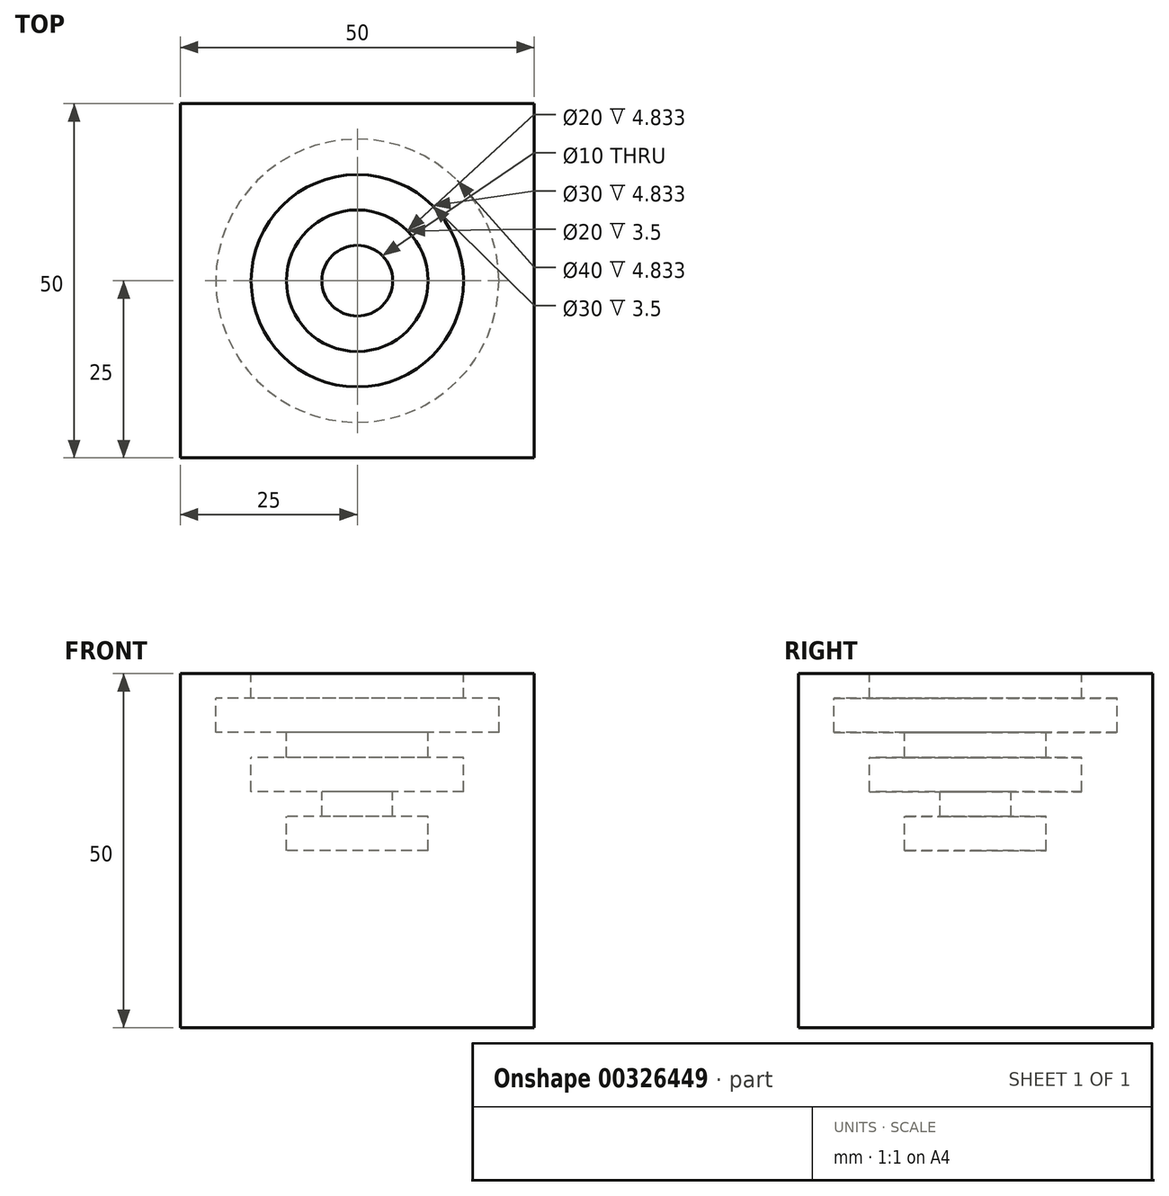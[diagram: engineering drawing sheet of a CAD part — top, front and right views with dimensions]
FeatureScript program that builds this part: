
annotation { "Feature Type Name" : "Feature", "Feature Type Description" : "" }
export const myFeature = defineFeature(function(context is Context, id is Id, definition is map)
    precondition{}
    {
        {
            var Q0;
            Q0=qCreatedBy(makeId("Top.planeOp"),FACE);
            var sketch = newSketch(context, id + "F0", { "sketchPlane" : qUnion([Q0])});
            skLineSegment(sketch, "E0.bottom", {"start": v(25, -25) * mm, "end": v(-25, -25) * mm});
            skLineSegment(sketch, "E0.top", {"start": v(25, 25) * mm, "end": v(-25, 25) * mm});
            skLineSegment(sketch, "E0.left", {"start": v(25, -25) * mm, "end": v(25, 25) * mm});
            skLineSegment(sketch, "E0.right", {"start": v(-25, -25) * mm, "end": v(-25, 25) * mm});
            skPoint(sketch, "E0.middle", {"position": v(0, 0) * mm});
            skSolve(sketch);
        }
        {
            var Q0;
            Q0=makeQuery(id+"F0.imprint","IMPRINT",FACE,{"disambiguationData":[TD([[makeQuery(id+"F0.imprint","IMPRINT",EDGE,{"derivedFrom":sQuery(id+"F0.wireOp",EDGE,"E0.bottom")}),-1.0]])]});
            extrude(context, id + "F1", {"entities" : qUnion([Q0]), "endBound" : BoundingType.SYMMETRIC, "depth" : 50 * mm});
        }
        {
            var Q0;
            Q0=qCreatedBy(makeId("Front.planeOp"),FACE);
            var sketch = newSketch(context, id + "F2", { "sketchPlane" : qUnion([Q0])});
            skLineSegment(sketch, "E1", {"start": v(0, 0) * mm, "end": v(0, 25) * mm});
            skLineSegment(sketch, "E2", {"start": v(0, 25) * mm, "end": v(15, 25) * mm});
            skLineSegment(sketch, "E3", {"start": v(15, 25) * mm, "end": v(15, 21.5) * mm});
            skLineSegment(sketch, "E4", {"start": v(15, 21.5) * mm, "end": v(20, 21.5) * mm});
            skLineSegment(sketch, "E5", {"start": v(20, 21.5) * mm, "end": v(20, 16.67) * mm});
            skLineSegment(sketch, "E6", {"start": v(20, 16.67) * mm, "end": v(10, 16.67) * mm});
            skLineSegment(sketch, "E7", {"start": v(10, 16.67) * mm, "end": v(10, 13.17) * mm});
            skLineSegment(sketch, "E8", {"start": v(10, 13.17) * mm, "end": v(15, 13.17) * mm});
            skLineSegment(sketch, "E9", {"start": v(15, 13.17) * mm, "end": v(15, 8.33) * mm});
            skLineSegment(sketch, "E10", {"start": v(15, 8.33) * mm, "end": v(5, 8.33) * mm});
            skLineSegment(sketch, "E11", {"start": v(5, 8.33) * mm, "end": v(5, 4.83) * mm});
            skLineSegment(sketch, "E12", {"start": v(5, 4.83) * mm, "end": v(10, 4.83) * mm});
            skLineSegment(sketch, "E13", {"start": v(10, 4.83) * mm, "end": v(10, 0) * mm});
            skLineSegment(sketch, "E14", {"start": v(10, 0) * mm, "end": v(0, 0) * mm});
            skSolve(sketch);
        }
        {
            var Q0;
            Q0 = qSketchRegion(id + "F2", true);
            var Q1;
            Q1=sQuery(id+"F2.wireOp",EDGE,"E1");
            revolve(context, id + "F3", {"operationType" : NewBodyOperationType.REMOVE, "entities" : qUnion([Q0]), "axis" : qUnion([Q1]), "revolveType" : RevolveType.FULL, "oppositeDirection" : true});
        }
        {
            var Q0;
            Q0=qCreatedBy(makeId("Top.planeOp"),FACE);
            var sketch = newSketch(context, id + "F4", { "sketchPlane" : qUnion([Q0])});
            skPoint(sketch, "E15.0", {"position": v(0, 25) * mm});
            skPoint(sketch, "E16.0", {"position": v(25, 0) * mm});
            skPoint(sketch, "E17.0", {"position": v(0, -25) * mm});
            skPoint(sketch, "E18.0", {"position": v(-25, 0) * mm});
            skLineSegment(sketch, "E19", {"start": v(-25, 0) * mm, "end": v(25, 0) * mm, "construction": true});
            skLineSegment(sketch, "E20", {"start": v(0, 25) * mm, "end": v(0, -25) * mm, "construction": true});
            skSolve(sketch);
        }
    });
